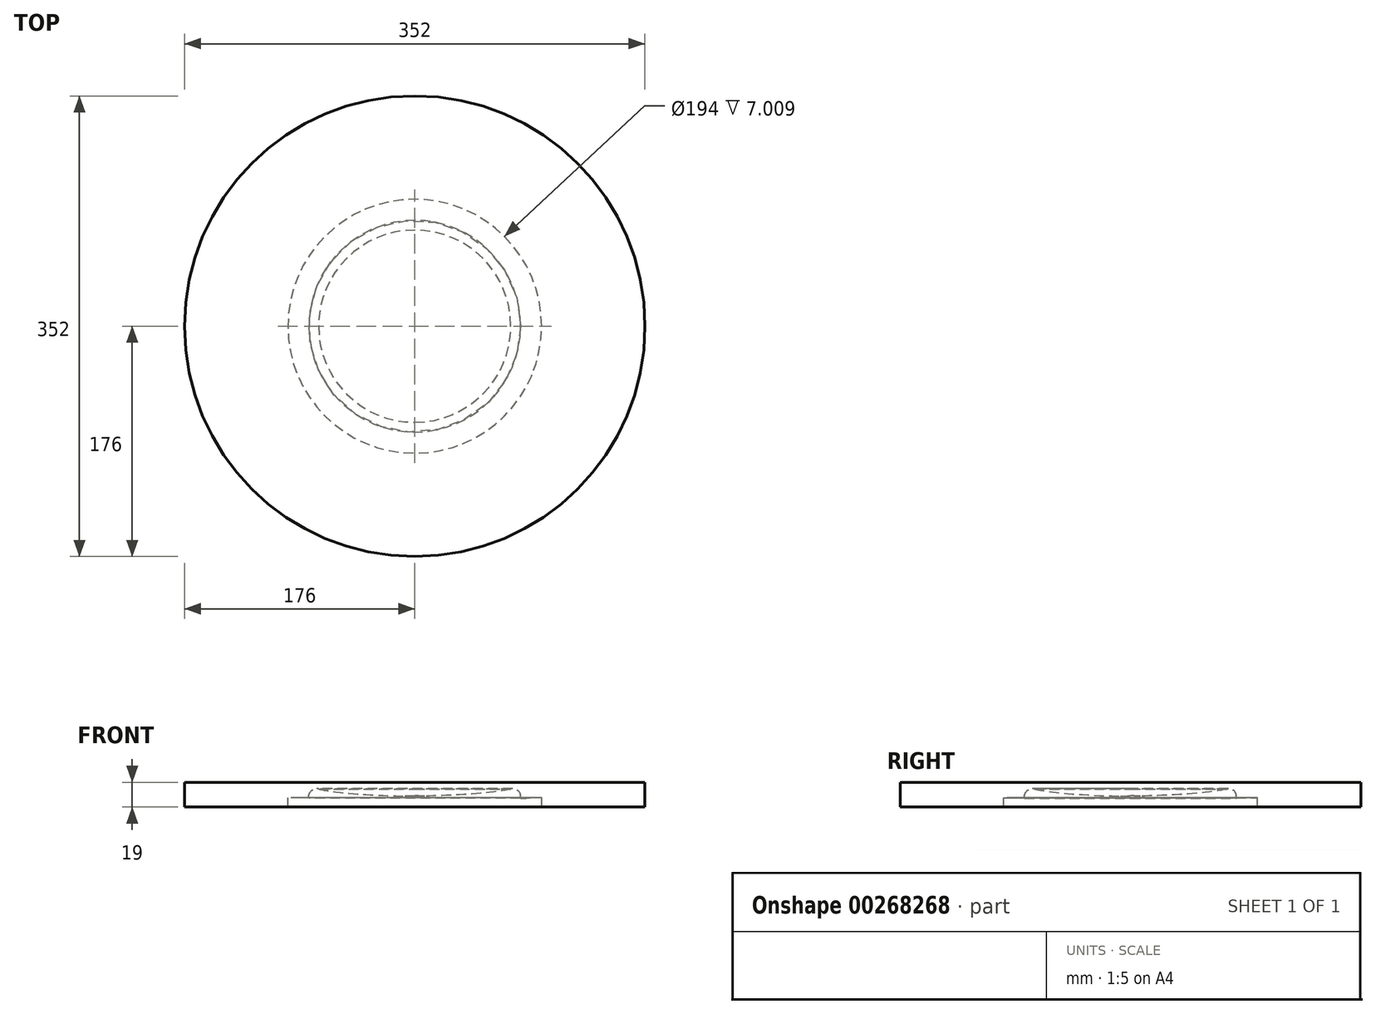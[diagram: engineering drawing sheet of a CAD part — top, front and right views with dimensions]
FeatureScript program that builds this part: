
annotation { "Feature Type Name" : "Feature", "Feature Type Description" : "" }
export const myFeature = defineFeature(function(context is Context, id is Id, definition is map)
    precondition{}
    {
        {
            var Q0;
            Q0=qCreatedBy(makeId("Right.planeOp"),FACE);
            var sketch = newSketch(context, id + "F0", { "sketchPlane" : qUnion([Q0])});
            skLineSegment(sketch, "E0", {"start": v(0, 9.26) * mm, "end": v(0, 9.26) * mm});
            skLineSegment(sketch, "E1.trimOffspring", {"start": v(-80, 13.39) * mm, "end": v(-80, 13.39) * mm});
            skPoint(sketch, "E2.visualSharp", {"position": v(-80, 13.39) * mm});
            skLineSegment(sketch, "E3", {"start": v(-176, 20.66) * mm, "end": v(0, 20.66) * mm});
            skLineSegment(sketch, "E4.0", {"start": v(-97, 1.66) * mm, "end": v(-176, 1.66) * mm});
            skFitSpline(sketch, "E4.1", {"points": [v(-80.98, 7.37) * mm, v(-81.1, 8) * mm, v(-81.28, 9.2) * mm, v(-81.37, 10.86) * mm, v(-81.29, 12.13) * mm, v(-81.12, 13.09) * mm, v(-80.88, 13.99) * mm, v(-80.53, 14.85) * mm, v(-79.96, 15.62) * mm, v(-79.39, 16.12) * mm, v(-78.8, 16.4) * mm, v(-78.27, 16.53) * mm, v(-77.88, 16.58) * mm, v(-77.5, 16.58) * mm, v(-76.98, 16.54) * mm, v(-76.35, 16.43) * mm, v(-75.6, 16.24) * mm, v(-74.65, 15.93) * mm, v(-73.53, 15.53) * mm, v(-72.53, 15.21) * mm, v(-71.6, 15) * mm, v(-70.5, 14.8) * mm, v(-68.98, 14.55) * mm, v(-67.1, 14.25) * mm, v(-64.83, 13.92) * mm, v(-62.22, 13.56) * mm, v(-59.27, 13.2) * mm, v(-56, 12.81) * mm, v(-52.44, 12.44) * mm, v(-48.58, 12.08) * mm, v(-43.1, 11.62) * mm, v(-35.74, 11.1) * mm, v(-26.48, 10.62) * mm, v(-17.15, 10.29) * mm, v(-8.15, 10.14) * mm, v(-2.61, 10.2) * mm, v(-0.03, 10.26) * mm]});
            skArc(sketch, "E4.2", {"start": v(-73.17, 15.42) * mm, "mid": v(-78.98, 14.2) * mm, "end": v(-80.9, 8.56) * mm});
            skLineSegment(sketch, "E4.3", {"start": v(-80.9, 8.56) * mm, "end": v(-92, 8.67) * mm});
            skLineSegment(sketch, "E5", {"start": v(-176, 1.66) * mm, "end": v(-176, 20.66) * mm});
            skLineSegment(sketch, "E6", {"start": v(-0.03, 10.26) * mm, "end": v(0, 10.26) * mm});
            skLineSegment(sketch, "E7", {"start": v(0, 10.26) * mm, "end": v(0, 20.66) * mm});
            skLineSegment(sketch, "E8", {"start": v(0, 47.7) * mm, "end": v(0, -14.34) * mm, "construction": true});
            skLineSegment(sketch, "E9", {"start": v(-97, 1.66) * mm, "end": v(-97, 8.67) * mm});
            skLineSegment(sketch, "E10", {"start": v(-92, 8.67) * mm, "end": v(-97, 8.67) * mm});
            skSolve(sketch);
        }
        {
            var Q0;
            Q0 = qSketchRegion(id + "F0", true);
            var Q1;
            Q1=sQuery(id+"F0.wireOp",EDGE,"E8");
            revolve(context, id + "F1", {"entities" : qUnion([Q0]), "axis" : qUnion([Q1]), "revolveType" : RevolveType.FULL});
        }
    });
